# Revit family: MHC-V5(7,9,12,14,16)WD2N8-C
name_source: partatom
category: Mechanical Equipment
revit_build: Autodesk Revit 2013 (Build: 20120221_2030(x64)
units: mm (PartAtom-declared; Revit-internal decimal feet)

## types (6) — shared parameters
Casing color = SB2403
Compressor = 1
Condensation = air
Depth = 410 mm
Description = Heat pump
Gas = R32
Height = 865 mm  [stored 2.83793 ft]
Installation = Outdoor installation
Manufacturer = Midea
Power supply = 220-240V 1N~50Hz
Series = M thermal Power
M thermal Power
M thermal Power
URL = https://mbt.midea.com
Width = 1040 mm  [stored 3.41207 ft]
clearance access behind = 300 mm  [stored 0.984252 ft]
clearance access left = 500 mm  [stored 1.64042 ft]
clearance access right = 500 mm  [stored 1.64042 ft]

## per-type parameters (varying)
| type | Air Flow | Cooling Power Input (EWT 23⁰C, LWT 18⁰C) | Cooling Power Input(EWT 12⁰C, LWT 7⁰C) | Cooling capacity (EWT 12⁰C, LWT 7⁰C) | Cooling capacity (EWT 23⁰C, LWT 18⁰C) | Heating Power Input (EWT 30⁰C, LWT 35⁰C) | Heating Power Input (EWT 40⁰C, LWT 45⁰C) | Heating capacity (EWT 30⁰C, LWT 35⁰C) | Heating capacity (EWT 40⁰C, LWT 45⁰C) | MOP (Maximum overcurrent protection) | Min cable selection (power wiring) | Minimum Circuit Amps | Net Weight | Water piping connections | clearance access front |
| MHC-V5WD2N8-C | 3900.00 m³/h | 1.28 kW | 1.69 kW | 5.50 kW | 6.50 kW | 1.23 kW | 1.65 kW | 6.50 kW | 6.60 kW | 4 A | 4mm2 | 13 A | 87.00 kg | 25.4 mm  [stored 0.0833333 ft] | 1000 mm  [stored 3.28084 ft] |
| MHC-V7WD2N8-C | 4500.00 m³/h | 1.71 kW | 2.53 kW | 7.40 kW | 8.30 kW | 1.66 kW | 2.24 kW | 8.40 kW | 8.50 kW | 4 A | 4mm2 | 15 A | 87.00 kg | 25.4 mm  [stored 0.0833333 ft] | 1000 mm  [stored 3.28084 ft] |
| MHC-V9WD2N8-C | 4500.00 m³/h | 2.33 kW | 3.10 kW | 9.00 kW | 10.00 kW | 2.22 kW | 2.80 kW | 10.00 kW | 10.20 kW | 4 A | 4mm2 | 16 A | 87.00 kg | 25.4 mm  [stored 0.0833333 ft] | 1000 mm  [stored 3.28084 ft] |
| MHC-V12WD2N8-C | 5200.00 m³/h | 2.65 kW | 3.74 kW | 11.60 kW | 12.20 kW | 2.49 kW | 3.39 kW | 12.20 kW | 12.50 kW | 6 A | 4mm2 | 25 A | 106.00 kg | 25.4 mm  [stored 0.0833333 ft] | 1500 mm  [stored 4.92126 ft] |
| MHC-V14WD2N8-C | 5200.00 m³/h | 3.16 kW | 4.57 kW | 13.40 kW | 13.90 kW | 3.00 kW | 4.09 kW | 14.10 kW | 14.50 kW | 6 A | 6mm2 | 27 A | 106.00 kg | 31.75 mm | 1500 mm  [stored 4.92126 ft] |
| MHC-V16WD2N8-C | 5200.00 m³/h | 3.67 kW | 4.83 kW | 14.00 kW | 15.40 kW | 3.56 kW | 4.70 kW | 16.00 kW | 16.20 kW | 6 A | 6mm2 | 28 A | 106.00 kg | 31.75 mm | 1500 mm  [stored 4.92126 ft] |

note: column(s) folded — value = type name in every type: Model

note: [stored X ft] marks values corroborated as IEEE doubles in the binary element streams (Revit-internal decimal feet)

## geometry (parser evidence)
native form markers: Blend x3, Sweep x26
no freeform markers — native parametric forms only
